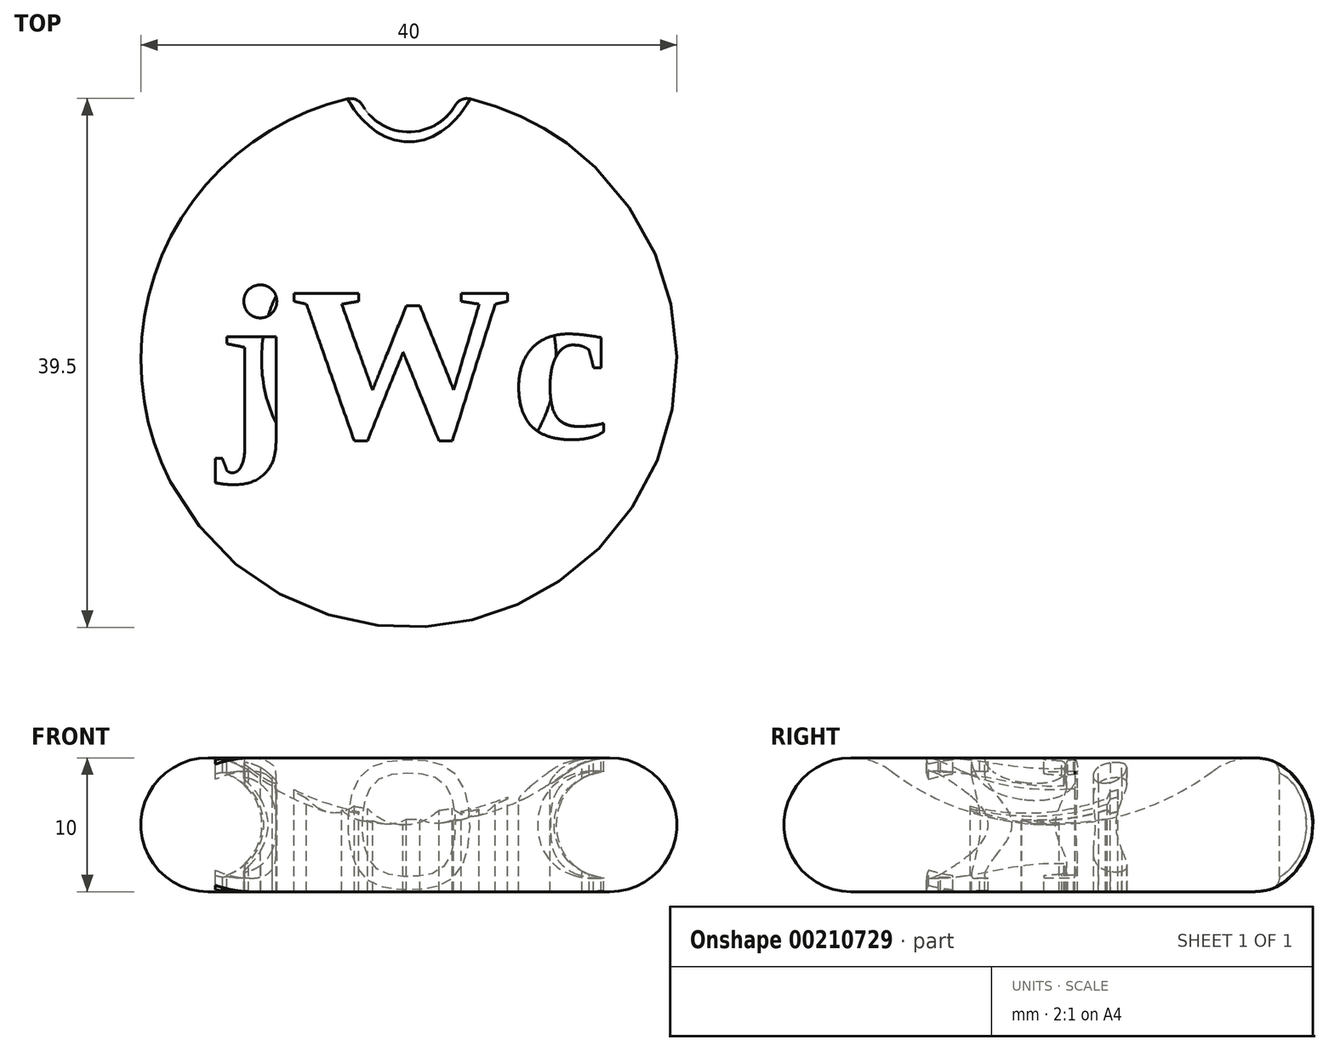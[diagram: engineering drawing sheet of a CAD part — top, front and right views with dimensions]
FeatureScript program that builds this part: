
annotation { "Feature Type Name" : "Feature", "Feature Type Description" : "" }
export const myFeature = defineFeature(function(context is Context, id is Id, definition is map)
    precondition{}
    {
        {
            var Q0;
            Q0=qCreatedBy(makeId("Front.planeOp"),FACE);
            var sketch = newSketch(context, id + "F0", { "sketchPlane" : qUnion([Q0])});
            skArc(sketch, "E0", {"start": v(-12, 9) * mm, "mid": v(-6.32, 6.03) * mm, "end": v(0, 5) * mm});
            skArc(sketch, "E1", {"start": v(-12, 9) * mm, "mid": v(-19.74, 6.58) * mm, "end": v(-15, 0) * mm});
            skLineSegment(sketch, "E2", {"start": v(-15, 0) * mm, "end": v(0, 0) * mm});
            skLineSegment(sketch, "E3", {"start": v(0, 0) * mm, "end": v(0, 5) * mm});
            skPoint(sketch, "E4.orphan", {"position": v(-17.66, 0) * mm});
            skSolve(sketch);
        }
        {
            var Q0;
            Q0=makeQuery(id+"F0.imprint","IMPRINT",FACE,{"disambiguationData":[TD([[makeQuery(id+"F0.imprint","IMPRINT",EDGE,{"derivedFrom":sQuery(id+"F0.wireOp",EDGE,"E0")}),-1.0]])]});
            var Q1;
            Q1=sQuery(id+"F0.wireOp",EDGE,"E3");
            revolve(context, id + "F1", {"entities" : qUnion([Q0]), "axis" : qUnion([Q1]), "revolveType" : RevolveType.FULL});
        }
        {
            var Q0;
            Q0=qCreatedBy(makeId("Top.planeOp"),FACE);
            cPlane(context, id + "F2", {"entities" : qUnion([Q0]), "cplaneType" : CPlaneType.OFFSET, "offset" : 10 * mm, "width" : 150 * mm, "height" : 150 * mm});
        }
        {
            var Q0;
            Q0=qCreatedBy(id+"F2.planeOp",FACE);
            var sketch = newSketch(context, id + "F3", { "sketchPlane" : qUnion([Q0])});
            skText(sketch, "E5", { "text": "jWc", "fontName": "Tinos-Bold.ttf"});
            const initialGuessF3  = {"E5": [-0.0143, -0.00584, 1, 0, 0.01185]};
            skSetInitialGuess(sketch, initialGuessF3);
            skSolve(sketch);
        }
        {
            var Q0;
            Q0 = qSketchRegion(id + "F3", true);
            extrude(context, id + "F4", {"entities" : qUnion([Q0]), "operationType" : NewBodyOperationType.REMOVE, "oppositeDirection" : true, "depth" : 50 * mm});
        }
        {
            var Q0;
            Q0=qCreatedBy(makeId("Front.planeOp"),FACE);
            var sketch = newSketch(context, id + "F5", { "sketchPlane" : qUnion([Q0])});
            skCircle(sketch, "E6", {"center": v(-15, 5) * mm, "radius": 4 * mm});
            skSolve(sketch);
        }
        {
            var Q0;
            Q0 = qSketchRegion(id + "F5", true);
            var Q1;
            Q1=sQuery(id+"F0.wireOp",EDGE,"E3");
            revolve(context, id + "F6", {"operationType" : NewBodyOperationType.ADD, "entities" : qUnion([Q0]), "axis" : qUnion([Q1]), "revolveType" : RevolveType.FULL});
        }
        {
            var Q0;
            Q0=qCreatedBy(id+"F2.planeOp",FACE);
            var sketch = newSketch(context, id + "F7", { "sketchPlane" : qUnion([Q0])});
            skCircle(sketch, "E7", {"center": v(0, 21) * mm, "radius": 4 * mm});
            skSolve(sketch);
        }
        {
            var Q0;
            Q0 = qSketchRegion(id + "F7", true);
            extrude(context, id + "F8", {"entities" : qUnion([Q0]), "operationType" : NewBodyOperationType.REMOVE, "oppositeDirection" : true, "depth" : 25 * mm});
        }
        {
            var Q0;
            Q0=makeQuery(id+"F8.boolean.opBoolean","INTERSECT",EDGE,{"derivedFrom":[makeQuery(id+"F1.opRevolve","SWEPT_FACE",FACE,{"disambiguationData":[OSD([sQuery(id+"F0.wireOp",EDGE,"E1")])]}),makeQuery(id+"F8.opExtrude","SWEPT_FACE",FACE,{"disambiguationData":[OSD([sQuery(id+"F7.wireOp",EDGE,"E7")])]})]});
            fillet(context, id + "F9", {"entities" : qUnion([Q0]), "radius" : 1 * mm, "tangentPropagation" : true, "allowEdgeOverflow" : false});
        }
    });
